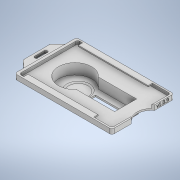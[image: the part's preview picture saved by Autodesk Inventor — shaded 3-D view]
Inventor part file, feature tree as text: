
AUTODESK INVENTOR PART (.ipt)
format: ipt  version: 2020 (Build 240168000, 168)  size: 944,640 bytes
history: native  units: mm
features: extrude x10, sketch x7, other x1, fillet x1
ambient origin geometry x8: Origin, YZ Plane, XZ Plane, XY Plane, X Axis, Y Axis, Z Axis, Center Point
bodies: Body1 (feature_tree)
feature tree (19):
  sketch  "Sketch1"  dims[d2=8.0mm d19=18.0mm]
  extrude  "OutsideFrame_Ex"  Depth=8.0mm
  extrude  "CardRidge"  Depth=2.0mm
  extrude  "TokenBuffer"  Depth=7.5mm
  extrude  "TokenCut"  Depth=1.5mm
  extrude  "LeftSlider"  Depth=1.5mm
  extrude  "RightSlider"  Depth=4.5mm TaperAngle=0.0deg
  sketch  "Sketch12"  dims[d37=1.5mm d40=1.5mm]
  other  "VersionNumber"
  extrude  "Extrusion15"  Depth=10.0mm TaperAngle=0.0deg
  extrude  "Extrusion16"  Depth=1.5mm
  extrude  "Extrusion17"  Depth=1.5mm
  extrude  "Extrusion19"  Depth=1.5mm
  fillet  "Fillet6"  Radius=1.5mm
  sketch  "Sketch4"  dims[d20=34.0mm d26=2.0mm]
  sketch  "Sketch5"  dims[d28=7.5mm d32=7.5mm]
  sketch  "Sketch6"  dims[d33=7.5mm d36=1.5mm]
  sketch  "Sketch15"  dims[d41=2.0mm d50=4.5mm d51=0.0mm]
  sketch  "Sketch22"  dims[d52=1.5mm d53=0.0mm d54=10.0mm d55=0.0mm d56=1.5mm d57=1.5mm d58=1.5mm d59=1.5mm d60=8.5mm d61=0.0mm d65=15.0mm d66=2.5mm d67=1.0mm d69=4.0mm d70=0.0mm d71=2.5mm d72=15.0mm d73=1.0mm d74=4.0mm d75=0.0mm d84=54.9mm d89=18.0mm d106=8.0mm d110=13.764568mm d113=1.0mm d114=0.0mm d116=1.5mm d122=3.604704mm d123=3.604704mm d128=3.5mm d129=0.0mm d130=1.0mm d131=0.0mm d152=34.0mm d153=1.5mm d154=0.0mm d155=25.0mm d163=15.7mm d164=15.7mm d165=27.45mm d166=27.45mm d167=8.5mm d171=26.535662mm d173=39.75mm d174=2.503179mm d177=86.9mm d178=0.624274mm d179=0.624274mm d182=4.0mm d183=4.0mm d187=3.0mm d188=1.6mm d189=1.6mm d190=2.5mm d191=2.5mm d192=8.0mm d193=6.5mm d194=6.5mm d195=6.55mm d196=6.55mm d202=15.799266mm d203=15.799266mm d204=23.79537mm d208=11.827268mm d215=0.0mm d216=18.0mm d217=3.0mm d218=0.75mm d219=0.0mm d220=2.0mm d42=0.872665mm d43=0.5mm d44=0.872665mm d45=0.872665mm d46=0.5mm d47=0.872665mm d76=0.5mm d77=0.872665mm d78=0.5mm d79=0.872665mm d80=0.872665mm d81=0.5mm d82=0.872665mm d111=0.5mm d112=0.872665mm d156=0.872665mm d221=0.5mm d222=0.872665mm d223=0.5mm d224=0.872665mm]
